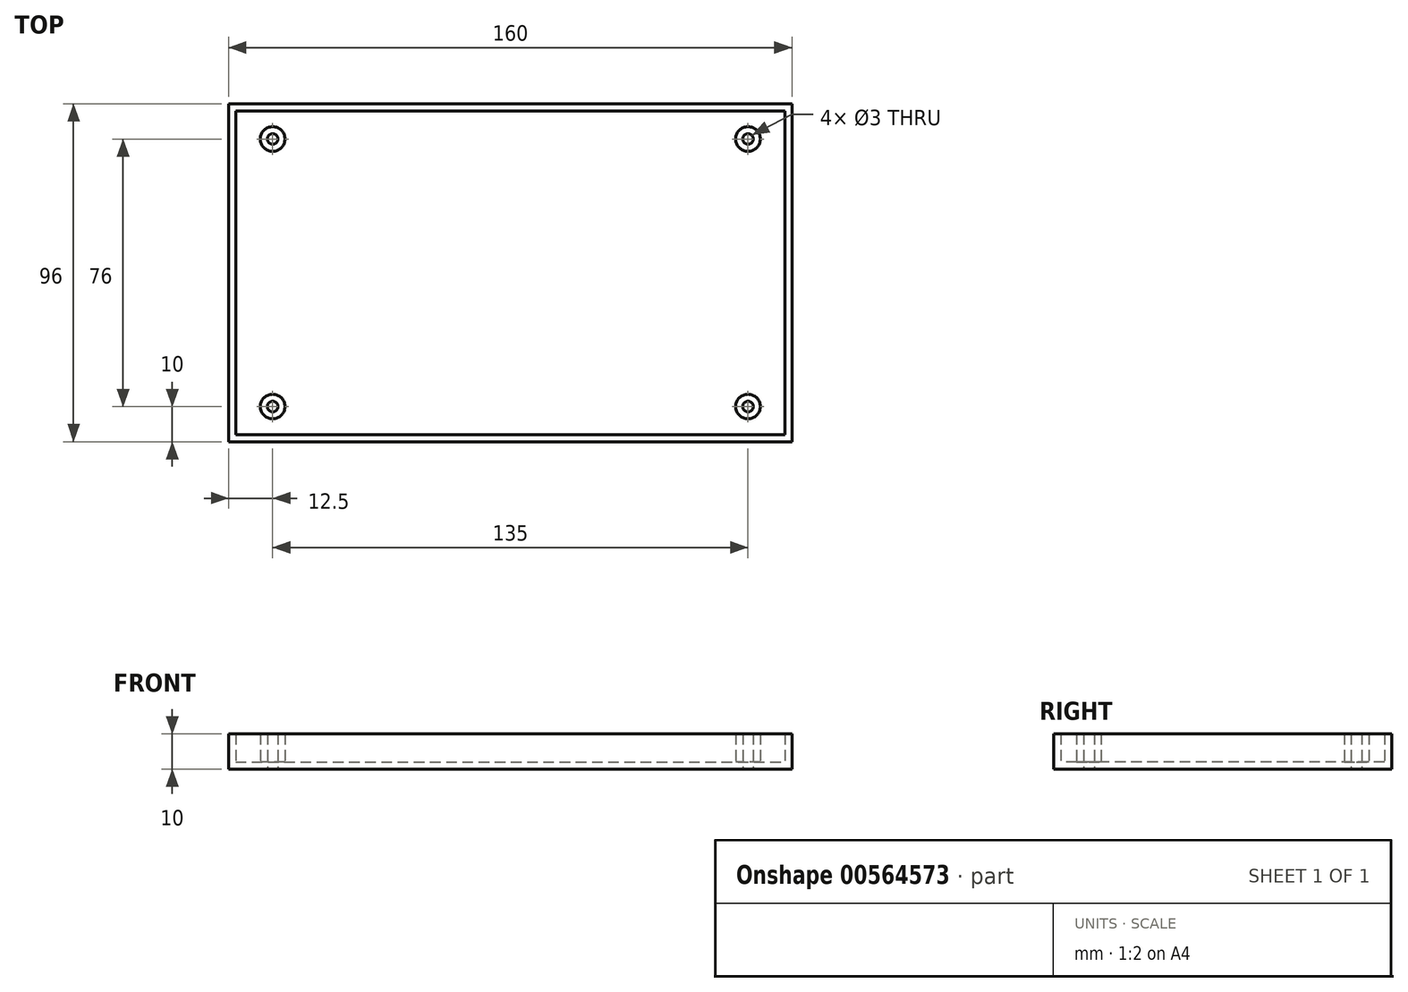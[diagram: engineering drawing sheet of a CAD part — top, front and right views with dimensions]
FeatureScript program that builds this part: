
annotation { "Feature Type Name" : "Feature", "Feature Type Description" : "" }
export const myFeature = defineFeature(function(context is Context, id is Id, definition is map)
    precondition{}
    {
        {
            var Q0;
            Q0=qCreatedBy(makeId("Top.planeOp"),FACE);
            var sketch = newSketch(context, id + "F0", { "sketchPlane" : qUnion([Q0])});
            skLineSegment(sketch, "E0.bottom", {"start": v(71.5, -42) * mm, "end": v(-71.5, -42) * mm});
            skLineSegment(sketch, "E0.top", {"start": v(71.5, 42) * mm, "end": v(-71.5, 42) * mm});
            skLineSegment(sketch, "E0.left", {"start": v(71.5, -42) * mm, "end": v(71.5, 42) * mm});
            skLineSegment(sketch, "E0.right", {"start": v(-71.5, -42) * mm, "end": v(-71.5, 42) * mm});
            skPoint(sketch, "E0.middle", {"position": v(0, 0) * mm});
            skCircle(sketch, "E1", {"center": v(-67.5, 38) * mm, "radius": 1.5 * mm});
            skCircle(sketch, "E2", {"center": v(67.5, 38) * mm, "radius": 1.5 * mm});
            skCircle(sketch, "E3", {"center": v(67.5, -38) * mm, "radius": 1.5 * mm});
            skCircle(sketch, "E4", {"center": v(-67.5, -38) * mm, "radius": 1.5 * mm});
            skLineSegment(sketch, "E5.bottom", {"start": v(-80, 48) * mm, "end": v(80, 48) * mm});
            skLineSegment(sketch, "E5.top", {"start": v(-80, -48) * mm, "end": v(80, -48) * mm});
            skLineSegment(sketch, "E5.left", {"start": v(-80, 48) * mm, "end": v(-80, -48) * mm});
            skLineSegment(sketch, "E5.right", {"start": v(80, 48) * mm, "end": v(80, -48) * mm});
            skSolve(sketch);
        }
        {
            var Q0;
            Q0=makeQuery(id+"F0.imprint","IMPRINT",FACE,{"disambiguationData":[TD([[makeQuery(id+"F0.imprint","IMPRINT",EDGE,{"derivedFrom":sQuery(id+"F0.wireOp",EDGE,"E0.bottom")}),1.0]])]});
            var Q1;
            Q1=makeQuery(id+"F0.imprint","IMPRINT",FACE,{"disambiguationData":[TD([[makeQuery(id+"F0.imprint","IMPRINT",EDGE,{"derivedFrom":sQuery(id+"F0.wireOp",EDGE,"E1")}),-1.0]])]});
            var Q2;
            Q2=makeQuery(id+"F0.imprint","IMPRINT",FACE,{"disambiguationData":[TD([[makeQuery(id+"F0.imprint","IMPRINT",EDGE,{"derivedFrom":sQuery(id+"F0.wireOp",EDGE,"E0.bottom")}),-1.0]])]});
            var Q3;
            Q3=makeQuery(id+"F0.imprint","IMPRINT",FACE,{"disambiguationData":[TD([[makeQuery(id+"F0.imprint","IMPRINT",EDGE,{"derivedFrom":sQuery(id+"F0.wireOp",EDGE,"E2")}),-1.0]])]});
            var Q4;
            Q4=makeQuery(id+"F0.imprint","IMPRINT",FACE,{"disambiguationData":[TD([[makeQuery(id+"F0.imprint","IMPRINT",EDGE,{"derivedFrom":sQuery(id+"F0.wireOp",EDGE,"E3")}),-1.0]])]});
            var Q5;
            Q5=makeQuery(id+"F0.imprint","IMPRINT",FACE,{"disambiguationData":[TD([[makeQuery(id+"F0.imprint","IMPRINT",EDGE,{"derivedFrom":sQuery(id+"F0.wireOp",EDGE,"E4")}),-1.0]])]});
            extrude(context, id + "F1", {"entities" : qUnion([Q0, Q1, Q2, Q3, Q4, Q5]), "depth" : 10 * mm, "offsetDistance" : 25 * mm});
        }
        {
            var Q0;
            Q0=makeQuery(id+"F1.opExtrude","CAP_FACE",FACE,{"disambiguationData":[OSD([sQuery(id+"F0.wireOp",EDGE,"E1"),sQuery(id+"F0.wireOp",EDGE,"E2"),sQuery(id+"F0.wireOp",EDGE,"E3"),sQuery(id+"F0.wireOp",EDGE,"E4"),sQuery(id+"F0.wireOp",EDGE,"E5.bottom"),sQuery(id+"F0.wireOp",EDGE,"E5.top"),sQuery(id+"F0.wireOp",EDGE,"E5.left"),sQuery(id+"F0.wireOp",EDGE,"E5.right")])],"isStart":false});
            shell(context, id + "F2", {"entities" : qUnion([Q0]), "thickness" : 2 * mm});
        }
    });
